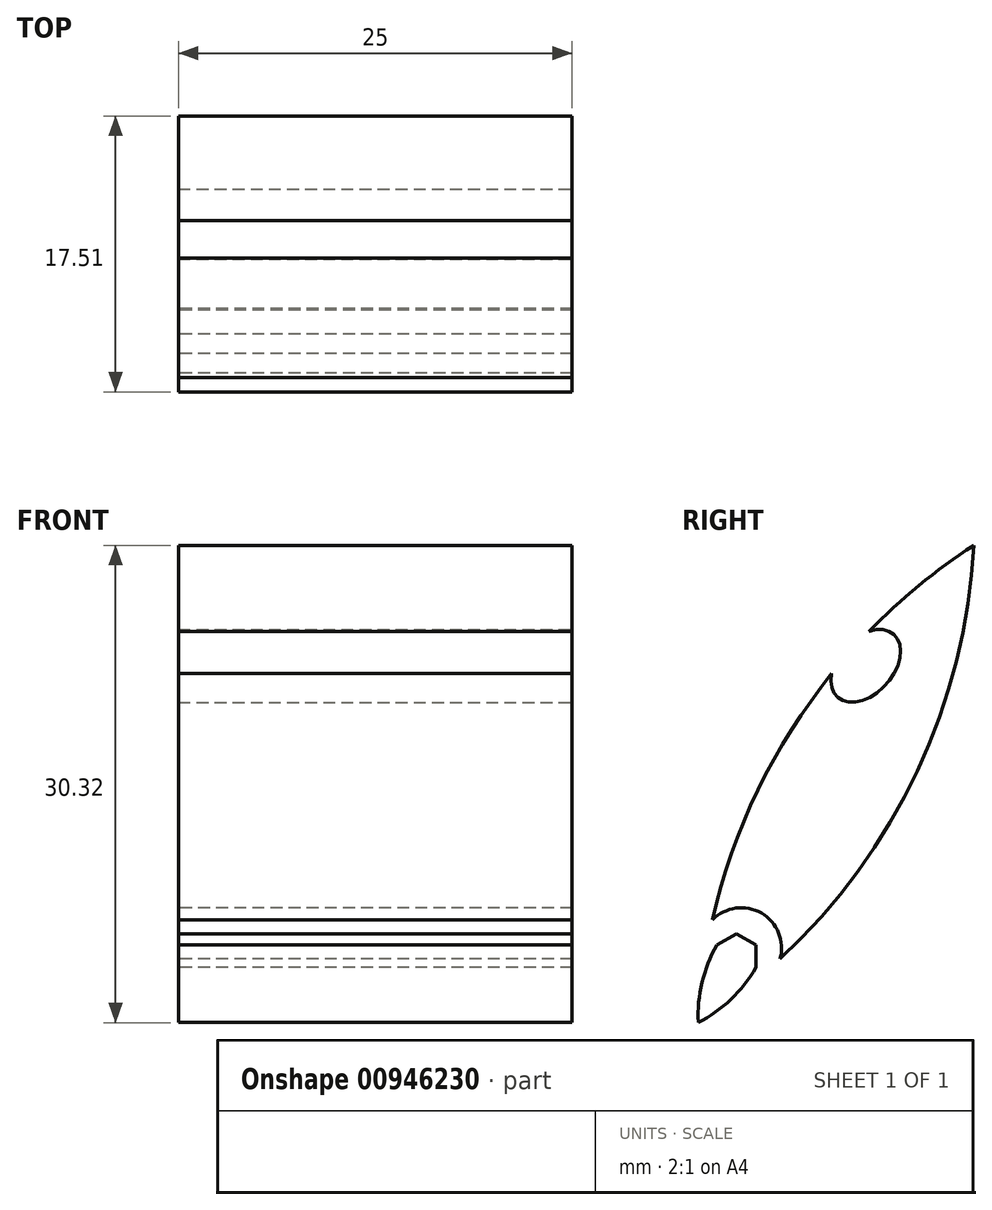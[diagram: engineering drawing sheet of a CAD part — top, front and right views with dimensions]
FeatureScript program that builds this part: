
annotation { "Feature Type Name" : "Feature", "Feature Type Description" : "" }
export const myFeature = defineFeature(function(context is Context, id is Id, definition is map)
    precondition{}
    {
        {
            var Q0;
            Q0=qCreatedBy(makeId("Right.planeOp"),FACE);
            var sketch = newSketch(context, id + "F0", { "sketchPlane" : qUnion([Q0])});
            skLineSegment(sketch, "E0", {"start": v(-5.08, -10.23) * mm, "end": v(-5.08, -11.66) * mm});
            skArc(sketch, "E1", {"start": v(8.75, 15.16) * mm, "mid": v(5.28, 12.61) * mm, "end": v(2.1, 9.7) * mm});
            skLineSegment(sketch, "E2", {"start": v(-6.32, -9.52) * mm, "end": v(-5.08, -10.23) * mm});
            skArc(sketch, "E3", {"start": v(-0.28, 7) * mm, "mid": v(-4.95, -0.38) * mm, "end": v(-7.85, -8.64) * mm});
            skArc(sketch, "E4", {"start": v(-7.56, -10.23) * mm, "mid": v(-8.5, -12.6) * mm, "end": v(-8.75, -15.16) * mm});
            skArc(sketch, "E5", {"start": v(-8.75, -15.16) * mm, "mid": v(-6.67, -13.67) * mm, "end": v(-5.08, -11.66) * mm});
            skLineSegment(sketch, "E6", {"start": v(-7.56, -10.23) * mm, "end": v(-6.32, -9.52) * mm});
            skEllipticalArc(sketch, "E7", {});
            skArc(sketch, "E8", {"start": v(-3.56, -11.11) * mm, "mid": v(-4.74, -8.2) * mm, "end": v(-7.85, -8.64) * mm});
            skArc(sketch, "E9", {"start": v(-3.56, -11.11) * mm, "mid": v(5.16, 0.82) * mm, "end": v(8.75, 15.16) * mm});
            skLineSegment(sketch, "E10", {"start": v(8.75, 15.16) * mm, "end": v(-8.75, -15.16) * mm, "construction": true});
            skPoint(sketch, "E11", {"position": v(0, 0) * mm});
            skCircle(sketch, "E12.cCircle", {"center": v(0, 0) * mm, "radius": 16 * mm, "construction": true});
            skLineSegment(sketch, "E12.0", {"start": v(-16, -16) * mm, "end": v(-16, 16) * mm});
            skLineSegment(sketch, "E12.1", {"start": v(-16, 16) * mm, "end": v(16, 16) * mm});
            skLineSegment(sketch, "E12.2", {"start": v(16, 16) * mm, "end": v(16, -16) * mm});
            skLineSegment(sketch, "E12.3", {"start": v(16, -16) * mm, "end": v(-16, -16) * mm});
            skPoint(sketch, "E12.0.midPoint", {"position": v(-16, 0) * mm});
            const initialGuessF0  = {"E7": [0.0018941338087106116, 0.007500391959287618, 0.667151986721845, 0.7449216244767602, 0.0026833365175593683, 0.0017473810671110486, 2.313906, 0.8451846928204135]};
            skSetInitialGuess(sketch, initialGuessF0);
            skSolve(sketch);
        }
        {
            var Q0;
            Q0=makeQuery(id+"F0.imprint","IMPRINT",FACE,{"disambiguationData":[TD([[makeQuery(id+"F0.imprint","IMPRINT",EDGE,{"derivedFrom":sQuery(id+"F0.wireOp",EDGE,"E1")}),1.0]])]});
            var Q1;
            Q1=makeQuery(id+"F0.imprint","IMPRINT",FACE,{"disambiguationData":[TD([[makeQuery(id+"F0.imprint","IMPRINT",EDGE,{"derivedFrom":sQuery(id+"F0.wireOp",EDGE,"E0")}),-1.0]])]});
            extrude(context, id + "F1", {"entities" : qUnion([Q0, Q1]), "depth" : 25 * mm, "offsetDistance" : 25 * mm});
        }
    });
